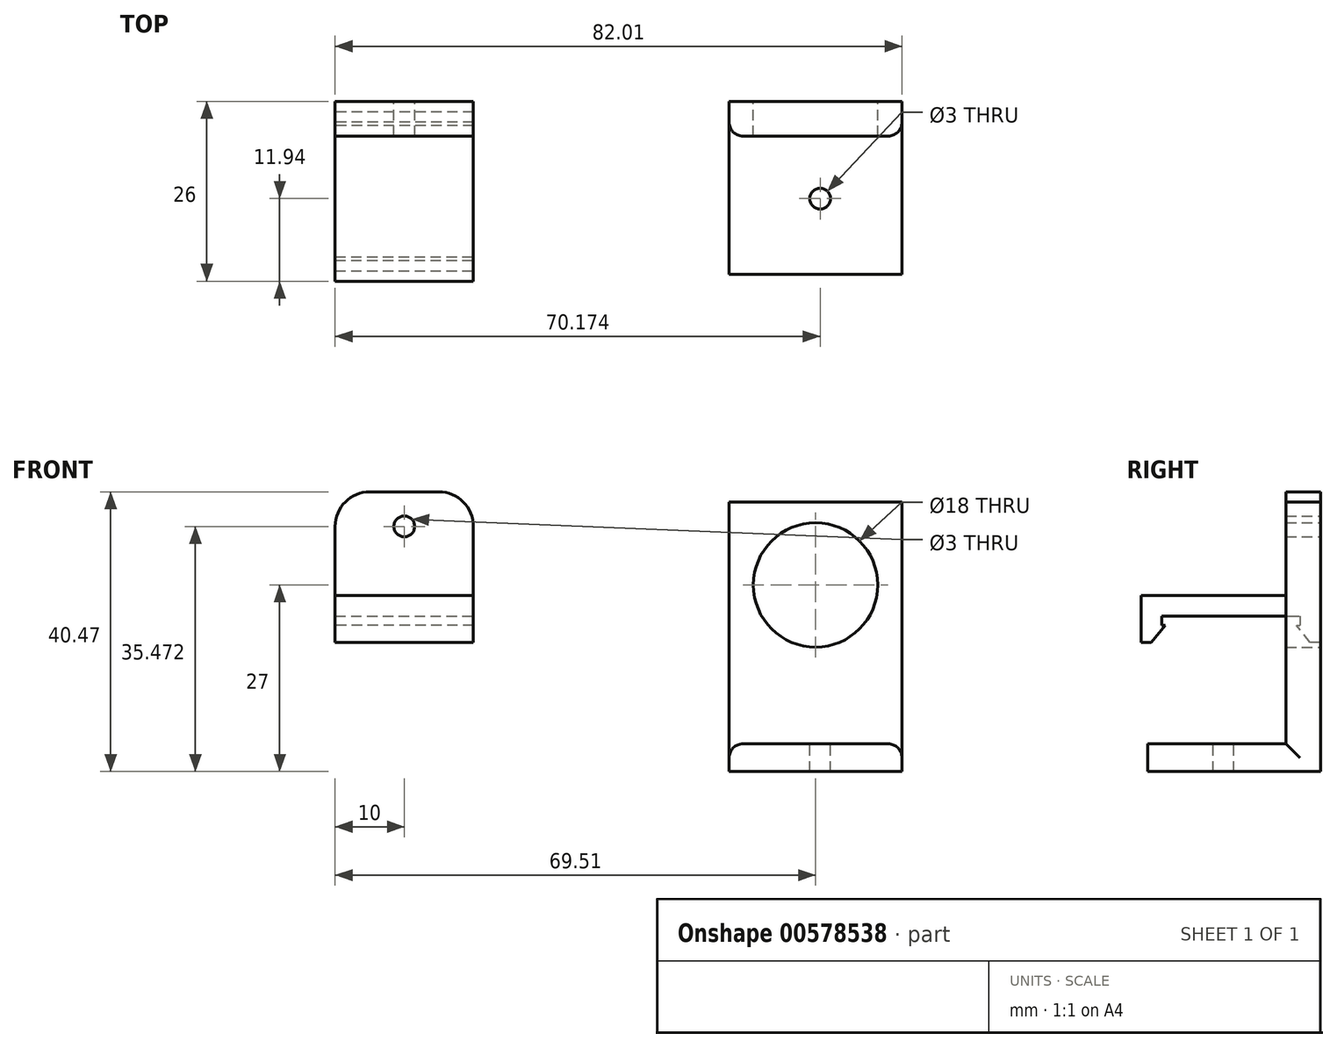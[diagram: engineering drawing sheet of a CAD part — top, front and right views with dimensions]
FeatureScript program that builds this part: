
annotation { "Feature Type Name" : "Feature", "Feature Type Description" : "" }
export const myFeature = defineFeature(function(context is Context, id is Id, definition is map)
    precondition{}
    {
        {
            var Q0;
            Q0=qCreatedBy(makeId("Front.planeOp"),FACE);
            var sketch = newSketch(context, id + "F0", { "sketchPlane" : qUnion([Q0])});
            skLineSegment(sketch, "E0", {"start": v(-57, 40.47) * mm, "end": v(-37, 40.47) * mm});
            skLineSegment(sketch, "E1", {"start": v(-37, 40.47) * mm, "end": v(-37, 25.47) * mm});
            skLineSegment(sketch, "E2", {"start": v(-57, 40.47) * mm, "end": v(-57, 25.47) * mm});
            skLineSegment(sketch, "E3", {"start": v(-57, 25.47) * mm, "end": v(-37, 25.47) * mm});
            skLineSegment(sketch, "E4", {"start": v(-37, 25.47) * mm, "end": v(-37, 22.47) * mm});
            skLineSegment(sketch, "E5", {"start": v(-37, 22.47) * mm, "end": v(-57, 22.47) * mm});
            skLineSegment(sketch, "E6", {"start": v(-57, 22.47) * mm, "end": v(-57, 25.47) * mm});
            skLineSegment(sketch, "E7", {"start": v(-37, 22.47) * mm, "end": v(-37, 21.17) * mm});
            skLineSegment(sketch, "E8", {"start": v(-37, 21.17) * mm, "end": v(-57, 21.17) * mm});
            skLineSegment(sketch, "E9", {"start": v(-57, 22.47) * mm, "end": v(-57, 21.17) * mm});
            skLineSegment(sketch, "E10", {"start": v(-57, 40.47) * mm, "end": v(-47, 40.47) * mm});
            skLineSegment(sketch, "E11", {"start": v(-47, 40.47) * mm, "end": v(-47, 35.47) * mm});
            skPoint(sketch, "E12", {"position": v(-47, 35.47) * mm});
            skCircle(sketch, "E13", {"center": v(-47, 35.47) * mm, "radius": 1.5 * mm});
            skSolve(sketch);
        }
        {
            var Q0;
            Q0=makeQuery(id+"F0.imprint","IMPRINT",FACE,{"disambiguationData":[TD([[makeQuery(id+"F0.imprint","IMPRINT",EDGE,{"derivedFrom":sQuery(id+"F0.wireOp",EDGE,"E0")}),-1.0]])]});
            extrude(context, id + "F1", {"entities" : qUnion([Q0]), "depth" : 5 * mm, "offsetDistance" : 25 * mm});
        }
        {
            var Q0;
            Q0=makeQuery(id+"F0.imprint","IMPRINT",FACE,{"disambiguationData":[TD([[makeQuery(id+"F0.imprint","IMPRINT",EDGE,{"derivedFrom":sQuery(id+"F0.wireOp",EDGE,"E3")}),-1.0]])]});
            extrude(context, id + "F2", {"entities" : qUnion([Q0]), "operationType" : NewBodyOperationType.ADD, "depth" : 26 * mm, "offsetDistance" : 25 * mm});
        }
        {
            var Q0;
            Q0=makeQuery(id+"F0.imprint","IMPRINT",FACE,{"disambiguationData":[TD([[makeQuery(id+"F0.imprint","IMPRINT",EDGE,{"derivedFrom":sQuery(id+"F0.wireOp",EDGE,"E5")}),1.0]])]});
            extrude(context, id + "F3", {"entities" : qUnion([Q0]), "operationType" : NewBodyOperationType.ADD, "depth" : 3 * mm, "offsetDistance" : 25 * mm});
        }
        {
            var Q0;
            Q0=makeQuery(id+"F2.opExtrude","SWEPT_FACE",FACE,{"disambiguationData":[OSD([sQuery(id+"F0.wireOp",EDGE,"E5")])]});
            var sketch = newSketch(context, id + "F4", { "sketchPlane" : qUnion([Q0])});
            skLineSegment(sketch, "E14", {"start": v(-57, 23) * mm, "end": v(-37, 23) * mm});
            skLineSegment(sketch, "E15", {"start": v(-37, 23) * mm, "end": v(-37, 26) * mm});
            skLineSegment(sketch, "E16", {"start": v(-57, 26) * mm, "end": v(-37, 26) * mm});
            skSolve(sketch);
        }
        {
            var Q0;
            {var subQ0=sQuery(id+"F4.wireOp",EDGE,"E14");Q0=makeQuery(id+"F4.imprint","IMPRINT",FACE,{"disambiguationData":[TD([[makeQuery(id+"F4.imprint","IMPRINT",EDGE,{"derivedFrom":subQ0}),1.0]])]});}
            extrude(context, id + "F5", {"entities" : qUnion([Q0]), "operationType" : NewBodyOperationType.ADD, "depth" : 1.3 * mm, "offsetDistance" : 25 * mm});
        }
        {
            var Q0;
            Q0=makeQuery(id+"F5.boolean.opBoolean","MERGE",FACE,{"derivedFrom":[makeQuery(id+"F3.boolean.opBoolean","MERGE",FACE,{"derivedFrom":[makeQuery(id+"F2.boolean.opBoolean","MERGE",FACE,{"derivedFrom":[makeQuery(id+"F1.opExtrude","SWEPT_FACE",FACE,{"disambiguationData":[OSD([sQuery(id+"F0.wireOp",EDGE,"E1")])]}),makeQuery(id+"F2.opExtrude","SWEPT_FACE",FACE,{"disambiguationData":[OSD([sQuery(id+"F0.wireOp",EDGE,"E4")])]})]}),makeQuery(id+"F3.opExtrude","SWEPT_FACE",FACE,{"disambiguationData":[OSD([sQuery(id+"F0.wireOp",EDGE,"E7")])]})]}),makeQuery(id+"F5.opExtrude","SWEPT_FACE",FACE,{"disambiguationData":[OSD([sQuery(id+"F4.wireOp",EDGE,"E15")])]})]});
            var sketch = newSketch(context, id + "F6", { "sketchPlane" : qUnion([Q0])});
            skLineSegment(sketch, "E17", {"start": v(-26, 21.17) * mm, "end": v(-26, 18.67) * mm});
            skLineSegment(sketch, "E18", {"start": v(-26, 18.67) * mm, "end": v(-24.5, 18.67) * mm});
            skLineSegment(sketch, "E19", {"start": v(-23, 21.17) * mm, "end": v(-22.5, 21.17) * mm});
            skLineSegment(sketch, "E20", {"start": v(-22.5, 21.17) * mm, "end": v(-24.5, 18.67) * mm});
            skSolve(sketch);
        }
        {
            var Q0;
            {var subQ0=sQuery(id+"F0.wireOp",EDGE,"E9");var subQ1=sQuery(id+"F0.wireOp",EDGE,"E6");Q0=makeQuery(id+"F5.boolean.opBoolean","MERGE",FACE,{"derivedFrom":[makeQuery(id+"F3.boolean.opBoolean","MERGE",FACE,{"derivedFrom":[makeQuery(id+"F2.boolean.opBoolean","MERGE",FACE,{"derivedFrom":[makeQuery(id+"F1.opExtrude","SWEPT_FACE",FACE,{"disambiguationData":[OSD([sQuery(id+"F0.wireOp",EDGE,"E2")])]}),makeQuery(id+"F2.opExtrude","SWEPT_FACE",FACE,{"disambiguationData":[OSD([subQ1])]})]}),makeQuery(id+"F3.opExtrude","SWEPT_FACE",FACE,{"disambiguationData":[OSD([subQ0])]})]}),makeQuery(id+"F5.opExtrude","SWEPT_FACE",FACE,{"disambiguationData":[OSD([sQuery(id+"F0.wireOp",EDGE,"E5"),subQ1,subQ0])]})]});}
            var sketch = newSketch(context, id + "F7", { "sketchPlane" : qUnion([Q0])});
            skLineSegment(sketch, "E21", {"start": v(22.5, 21.18) * mm, "end": v(26, 21.17) * mm});
            skLineSegment(sketch, "E22", {"start": v(0, 21.17) * mm, "end": v(0, 18.67) * mm});
            skLineSegment(sketch, "E23", {"start": v(0, 21.17) * mm, "end": v(3.5, 21.17) * mm});
            skLineSegment(sketch, "E24", {"start": v(0, 18.67) * mm, "end": v(1.5, 18.67) * mm});
            skLineSegment(sketch, "E25", {"start": v(1.5, 18.67) * mm, "end": v(3.5, 21.17) * mm});
            skSolve(sketch);
        }
        {
            var Q0;
            Q0=makeQuery(id+"F6.imprint","IMPRINT",FACE,{"disambiguationData":[TD([[makeQuery(id+"F6.imprint","IMPRINT",EDGE,{"derivedFrom":sQuery(id+"F6.wireOp",EDGE,"E17")}),1.0]])]});
            extrude(context, id + "F8", {"entities" : qUnion([Q0]), "operationType" : NewBodyOperationType.ADD, "depth" : -20 * mm, "offsetDistance" : 25 * mm});
        }
        {
            var Q0;
            {var subQ4=sQuery(id+"F7.wireOp",EDGE,"E22");Q0=makeQuery(id+"F7.imprint","IMPRINT",FACE,{"disambiguationData":[TD([[makeQuery(id+"F7.imprint","IMPRINT",EDGE,{"derivedFrom":subQ4}),1.0]])]});}
            extrude(context, id + "F9", {"entities" : qUnion([Q0]), "operationType" : NewBodyOperationType.ADD, "depth" : -20 * mm, "offsetDistance" : 25 * mm});
        }
        {
            var Q0;
            Q0=makeQuery(id+"F1.opExtrude","SWEPT_EDGE",EDGE,{"disambiguationData":[OSD([sQuery(id+"F0.wireOp",EDGE,"E0"),sQuery(id+"F0.wireOp",EDGE,"E2")])]});
            fillet(context, id + "F10", {"entities" : qUnion([Q0]), "radius" : 5 * mm, "tangentPropagation" : true, "allowEdgeOverflow" : false});
        }
        {
            var Q0;
            Q0=makeQuery(id+"F1.opExtrude","SWEPT_EDGE",EDGE,{"disambiguationData":[OSD([sQuery(id+"F0.wireOp",EDGE,"E0"),sQuery(id+"F0.wireOp",EDGE,"E1")])]});
            fillet(context, id + "F11", {"entities" : qUnion([Q0]), "radius" : 5 * mm, "tangentPropagation" : true, "allowEdgeOverflow" : false});
        }
        {
            var Q0;
            Q0=qCreatedBy(makeId("Front.planeOp"),FACE);
            var sketch = newSketch(context, id + "F12", { "sketchPlane" : qUnion([Q0])});
            skLineSegment(sketch, "E26", {"start": v(0, 0) * mm, "end": v(0, 4) * mm});
            skLineSegment(sketch, "E27", {"start": v(0, 4) * mm, "end": v(25, 4) * mm});
            skLineSegment(sketch, "E28", {"start": v(25, 4) * mm, "end": v(25, 0) * mm});
            skLineSegment(sketch, "E29", {"start": v(0, 0) * mm, "end": v(25, 0) * mm});
            skLineSegment(sketch, "E30", {"start": v(0, 4) * mm, "end": v(0, 39) * mm});
            skLineSegment(sketch, "E31", {"start": v(0, 39) * mm, "end": v(25, 39) * mm});
            skLineSegment(sketch, "E32", {"start": v(25, 39) * mm, "end": v(25, 4) * mm});
            skLineSegment(sketch, "E33", {"start": v(0, 0) * mm, "end": v(0, 18) * mm});
            skLineSegment(sketch, "E34", {"start": v(0, 18) * mm, "end": v(12.5, 18) * mm});
            skLineSegment(sketch, "E35", {"start": v(12.5, 18) * mm, "end": v(12.5, 27) * mm});
            skCircle(sketch, "E36", {"center": v(12.5, 27) * mm, "radius": 9 * mm});
            skSolve(sketch);
        }
        {
            var Q0;
            {var subQ0=sQuery(id+"F12.wireOp",EDGE,"E27");Q0=makeQuery(id+"F12.imprint","IMPRINT",FACE,{"disambiguationData":[TD([[makeQuery(id+"F12.imprint","IMPRINT",EDGE,{"derivedFrom":subQ0}),-1.0]])]});}
            extrude(context, id + "F13", {"entities" : qUnion([Q0]), "depth" : 25 * mm, "offsetDistance" : 25 * mm});
        }
        {
            var Q0;
            {var subQ1=sQuery(id+"F12.wireOp",EDGE,"E27");Q0=makeQuery(id+"F12.imprint","IMPRINT",FACE,{"disambiguationData":[TD([[makeQuery(id+"F12.imprint","IMPRINT",EDGE,{"derivedFrom":subQ1}),1.0]])]});}
            extrude(context, id + "F14", {"entities" : qUnion([Q0]), "operationType" : NewBodyOperationType.ADD, "depth" : 5 * mm, "offsetDistance" : 25 * mm});
        }
        {
            var Q0;
            Q0=makeQuery(id+"F13.opExtrude","SWEPT_FACE",FACE,{"disambiguationData":[OSD([sQuery(id+"F12.wireOp",EDGE,"E27")])]});
            var sketch = newSketch(context, id + "F15", { "sketchPlane" : qUnion([Q0])});
            skCircle(sketch, "E37", {"center": v(13.16, -14.06) * mm, "radius": 1.5 * mm});
            skSolve(sketch);
        }
        {
            var Q0;
            Q0=sQuery(id+"F15.wireOp",VERTEX,"E37.center");
            var Q1;
            Q1=makeQuery(id+"F13.opExtrude","SWEPT_BODY",BODY,{"disambiguationData":[OSD([sQuery(id+"F12.wireOp",EDGE,"E27"),sQuery(id+"F12.wireOp",EDGE,"E28"),sQuery(id+"F12.wireOp",EDGE,"E29"),sQuery(id+"F12.wireOp",EDGE,"E33")])]});
            hole(context, id + "F16", {"style" : HoleStyle.SIMPLE, "endStyle" : HoleEndStyle.THROUGH, "holeDiameter" : 3 * mm, "majorDiameter" : 5 * mm, "isTappedThrough" : true, "tappedDepth" : 12 * mm, "tapClearance" : 3, "locations" : qUnion([Q0]), "scope" : qUnion([Q1])});
        }
        {
            var Q0;
            Q0=makeQuery(id+"F13.opExtrude","SWEPT_EDGE",EDGE,{"disambiguationData":[OSD([sQuery(id+"F12.wireOp",EDGE,"E27"),sQuery(id+"F12.wireOp",EDGE,"E28"),sQuery(id+"F12.wireOp",EDGE,"E32")])]});
            var Q1;
            Q1=makeQuery(id+"F14.opExtrude","CAP_EDGE",EDGE,{"disambiguationData":[OSD([sQuery(id+"F12.wireOp",EDGE,"E32")])],"isStart":false});
            fillet(context, id + "F17", {"entities" : qUnion([Q0, Q1]), "radius" : 2 * mm, "tangentPropagation" : true, "allowEdgeOverflow" : false});
        }
        {
            var Q0;
            Q0=makeQuery(id+"F14.opExtrude","CAP_EDGE",EDGE,{"disambiguationData":[OSD([sQuery(id+"F12.wireOp",EDGE,"E30"),sQuery(id+"F12.wireOp",EDGE,"E33")])],"isStart":false});
            var Q1;
            Q1=makeQuery(id+"F13.opExtrude","SWEPT_EDGE",EDGE,{"disambiguationData":[OSD([sQuery(id+"F12.wireOp",EDGE,"E27"),sQuery(id+"F12.wireOp",EDGE,"E33")])]});
            fillet(context, id + "F18", {"entities" : qUnion([Q0, Q1]), "radius" : 2 * mm, "tangentPropagation" : true, "allowEdgeOverflow" : false});
        }
    });
